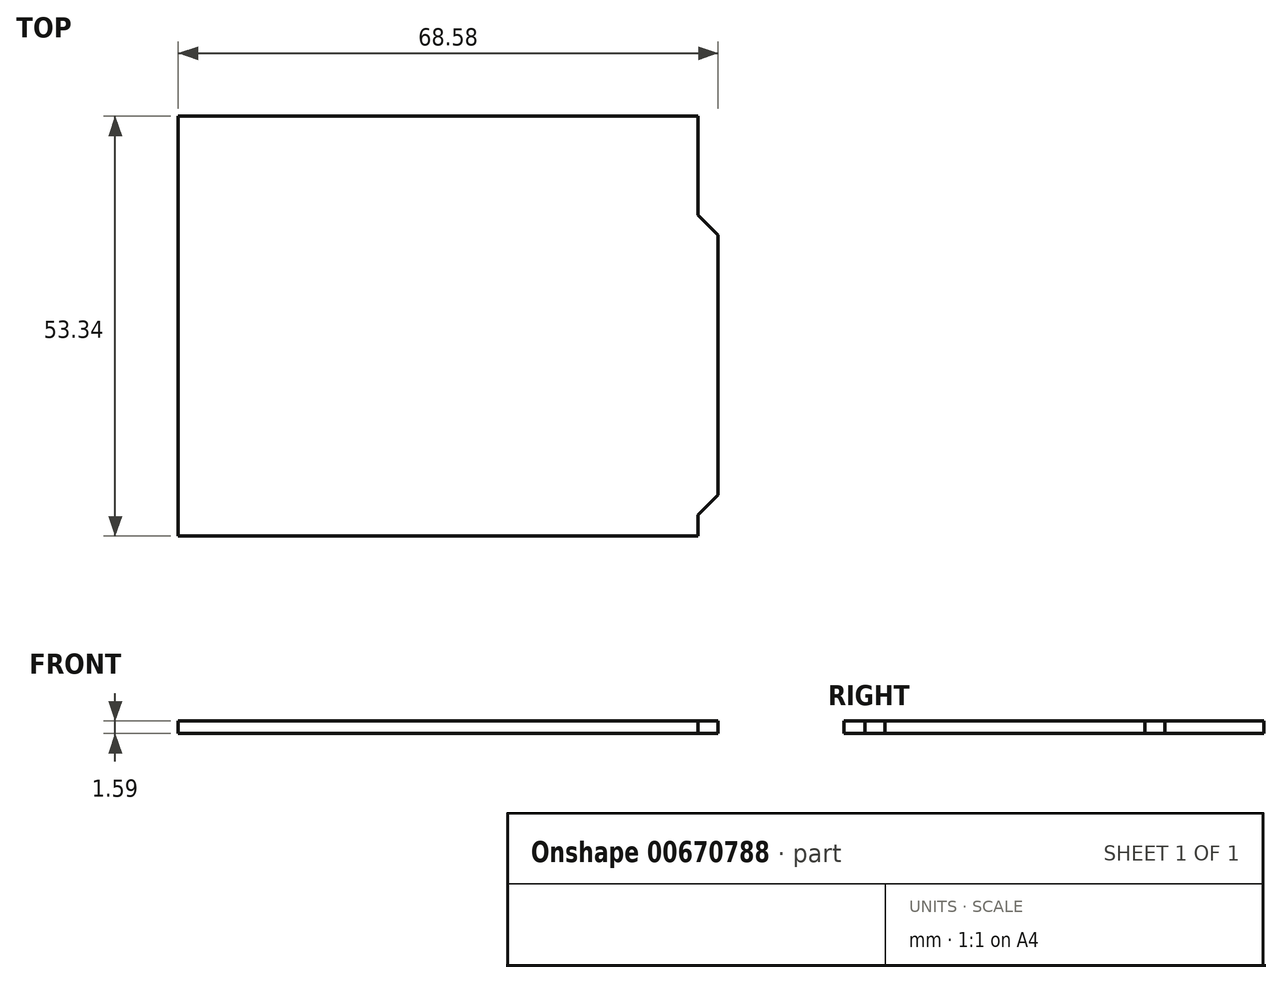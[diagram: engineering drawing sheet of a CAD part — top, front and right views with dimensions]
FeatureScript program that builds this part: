
annotation { "Feature Type Name" : "Feature", "Feature Type Description" : "" }
export const myFeature = defineFeature(function(context is Context, id is Id, definition is map)
    precondition{}
    {
        {
            var Q0;
            Q0=qCreatedBy(makeId("Top.planeOp"),FACE);
            var sketch = newSketch(context, id + "F0", { "sketchPlane" : qUnion([Q0])});
            skLineSegment(sketch, "E0", {"start": v(-15.11, 15.11) * mm, "end": v(50.93, 15.11) * mm});
            skLineSegment(sketch, "E1", {"start": v(50.93, 15.11) * mm, "end": v(50.93, -38.23) * mm});
            skLineSegment(sketch, "E2", {"start": v(50.93, -38.23) * mm, "end": v(-15.11, -38.23) * mm});
            skLineSegment(sketch, "E3", {"start": v(-15.11, -38.23) * mm, "end": v(-15.11, 15.11) * mm});
            skLineSegment(sketch, "E4", {"start": v(0, 0) * mm, "end": v(0, 15.11) * mm, "construction": true});
            skLineSegment(sketch, "E5", {"start": v(0, 0) * mm, "end": v(-15.11, 0) * mm, "construction": true});
            skLineSegment(sketch, "E6", {"start": v(50.93, -35.56) * mm, "end": v(53.47, -33.02) * mm});
            skLineSegment(sketch, "E7", {"start": v(53.47, -33.02) * mm, "end": v(53.47, 0) * mm});
            skLineSegment(sketch, "E8", {"start": v(50.93, 2.54) * mm, "end": v(53.47, 0) * mm});
            skSolve(sketch);
        }
        {
            var Q0;
            Q0 = qSketchRegion(id + "F0", true);
            extrude(context, id + "F1", {"entities" : qUnion([Q0]), "depth" : 1.59 * mm, "offsetDistance" : 25 * mm});
        }
    });
